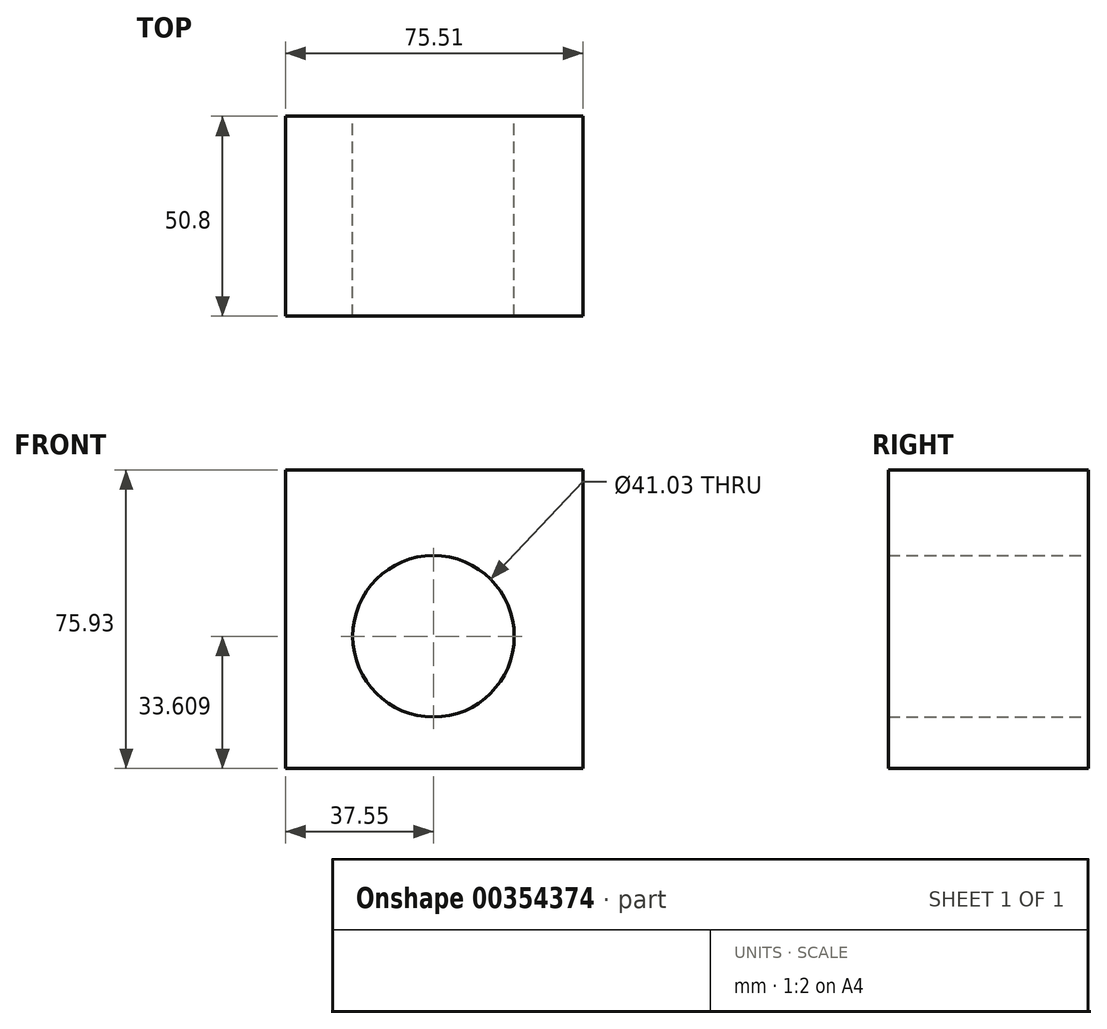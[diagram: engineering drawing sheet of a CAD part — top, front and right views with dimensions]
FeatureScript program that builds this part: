
annotation { "Feature Type Name" : "Feature", "Feature Type Description" : "" }
export const myFeature = defineFeature(function(context is Context, id is Id, definition is map)
    precondition{}
    {
        {
            var Q0;
            Q0=qCreatedBy(makeId("Front.planeOp"),FACE);
            var sketch = newSketch(context, id + "F0", { "sketchPlane" : qUnion([Q0])});
            skCircle(sketch, "E0", {"center": v(37.55, -42.32) * mm, "radius": 20.52 * mm});
            skLineSegment(sketch, "E1.bottom", {"start": v(0, -75.93) * mm, "end": v(75.51, -75.93) * mm});
            skLineSegment(sketch, "E1.top", {"start": v(0, 0) * mm, "end": v(75.51, 0) * mm});
            skLineSegment(sketch, "E1.left", {"start": v(0, -75.93) * mm, "end": v(0, 0) * mm});
            skLineSegment(sketch, "E1.right", {"start": v(75.51, -75.93) * mm, "end": v(75.51, 0) * mm});
            skSolve(sketch);
        }
        {
            var Q0;
            Q0 = qSketchRegion(id + "F0", true);
            extrude(context, id + "F1", {"entities" : qUnion([Q0]), "depth" : 50.8 * mm});
        }
    });
